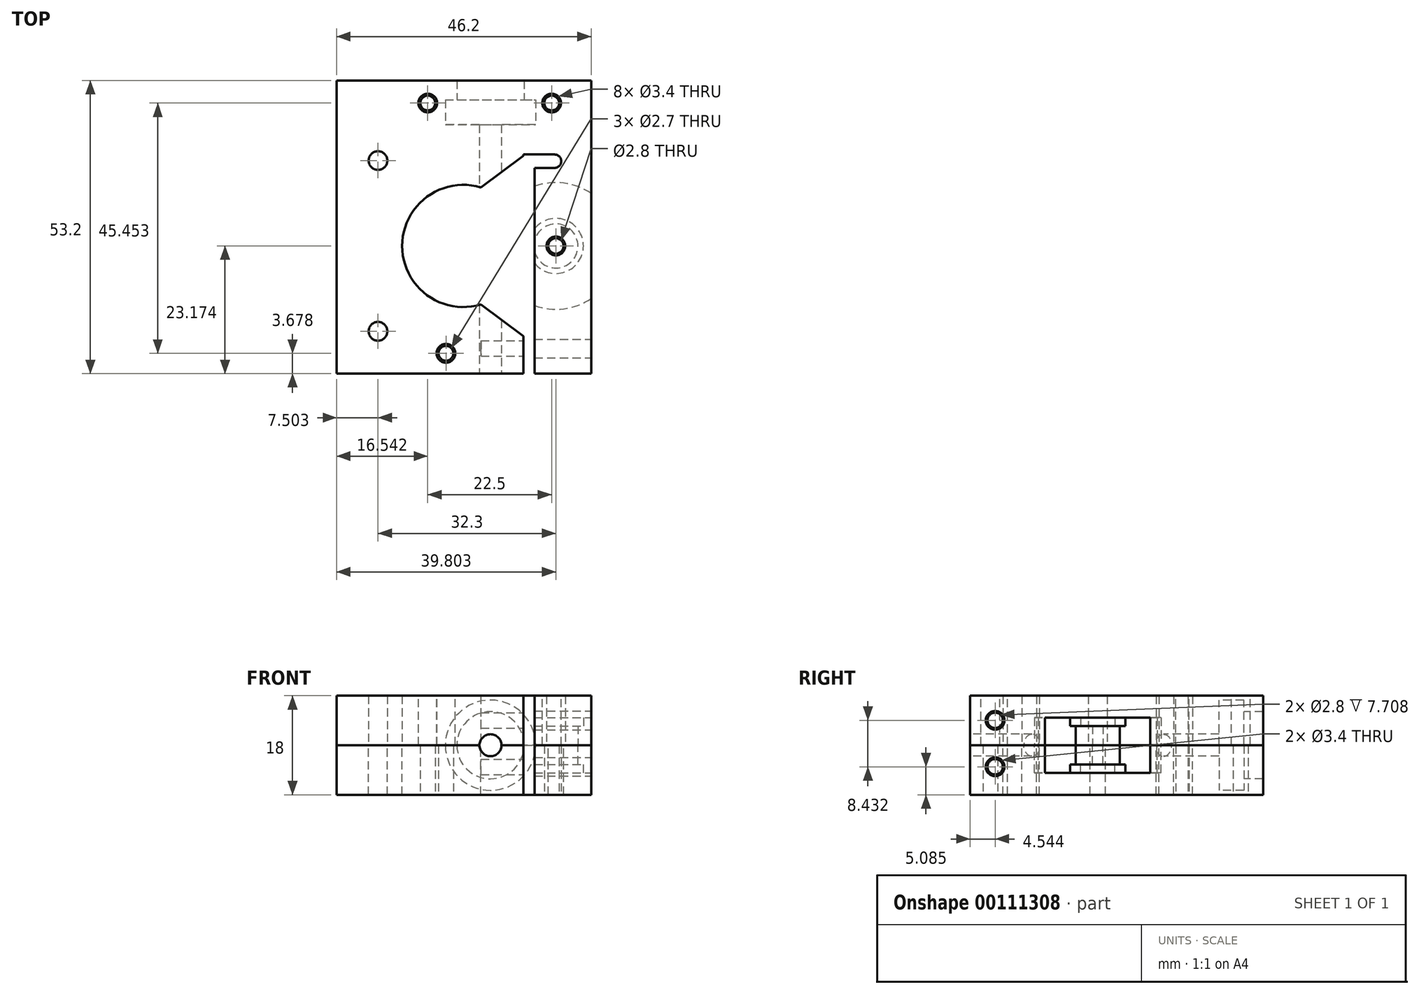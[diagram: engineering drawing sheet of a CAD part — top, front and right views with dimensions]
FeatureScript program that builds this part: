
annotation { "Feature Type Name" : "Feature", "Feature Type Description" : "" }
export const myFeature = defineFeature(function(context is Context, id is Id, definition is map)
    precondition{}
    {
        {
            var Q0;
            Q0=qCreatedBy(makeId("Top.planeOp"),FACE);
            var sketch = newSketch(context, id + "F0", { "sketchPlane" : qUnion([Q0])});
            skLineSegment(sketch, "E0", {"start": v(-24.43, 35.85) * mm, "end": v(-24.43, -17.36) * mm});
            skLineSegment(sketch, "E1", {"start": v(-24.43, -17.36) * mm, "end": v(-24.43, -17.36) * mm});
            skLineSegment(sketch, "E2", {"start": v(-24.43, -17.36) * mm, "end": v(-24.43, -17.35) * mm});
            skLineSegment(sketch, "E3", {"start": v(-24.43, -17.35) * mm, "end": v(9.48, -17.35) * mm});
            skLineSegment(sketch, "E4", {"start": v(9.48, -17.35) * mm, "end": v(9.48, 22.43) * mm});
            skLineSegment(sketch, "E5", {"start": v(9.48, 22.43) * mm, "end": v(15.14, 22.43) * mm});
            skLineSegment(sketch, "E6", {"start": v(15.14, 20) * mm, "end": v(11.48, 20) * mm});
            skLineSegment(sketch, "E7", {"start": v(11.48, 20) * mm, "end": v(11.48, -17.35) * mm});
            skLineSegment(sketch, "E8", {"start": v(11.48, -17.35) * mm, "end": v(21.77, -17.35) * mm});
            skLineSegment(sketch, "E9", {"start": v(21.77, -17.35) * mm, "end": v(21.77, 35.85) * mm});
            skLineSegment(sketch, "E10", {"start": v(21.77, 35.85) * mm, "end": v(-24.43, 35.85) * mm});
            skCircle(sketch, "E11", {"center": v(-7.89, 31.78) * mm, "radius": 1.35 * mm});
            skCircle(sketch, "E12", {"center": v(14.61, 31.78) * mm, "radius": 1.35 * mm});
            skCircle(sketch, "E13", {"center": v(-4.59, -13.67) * mm, "radius": 1.35 * mm});
            skArc(sketch, "E14", {"start": v(15.14, 20) * mm, "mid": v(16.35, 21.21) * mm, "end": v(15.14, 22.43) * mm});
            skCircle(sketch, "E15", {"center": v(-7.89, 31.78) * mm, "radius": 1.7 * mm});
            skCircle(sketch, "E16", {"center": v(14.61, 31.78) * mm, "radius": 1.7 * mm});
            skCircle(sketch, "E17", {"center": v(-4.59, -13.67) * mm, "radius": 1.7 * mm});
            skSolve(sketch);
        }
        {
            var Q0;
            Q0=makeQuery(id+"F0.imprint","IMPRINT",FACE,{"disambiguationData":[TD([[makeQuery(id+"F0.imprint","IMPRINT",EDGE,{"derivedFrom":sQuery(id+"F0.wireOp",EDGE,"E0")}),1.0]])]});
            var Q1;
            Q1=makeQuery(id+"F0.imprint","IMPRINT",FACE,{"disambiguationData":[TD([[makeQuery(id+"F0.imprint","IMPRINT",EDGE,{"derivedFrom":sQuery(id+"F0.wireOp",EDGE,"E11")}),-1.0]])]});
            var Q2;
            Q2=makeQuery(id+"F0.imprint","IMPRINT",FACE,{"disambiguationData":[TD([[makeQuery(id+"F0.imprint","IMPRINT",EDGE,{"derivedFrom":sQuery(id+"F0.wireOp",EDGE,"E12")}),-1.0]])]});
            var Q3;
            Q3=makeQuery(id+"F0.imprint","IMPRINT",FACE,{"disambiguationData":[TD([[makeQuery(id+"F0.imprint","IMPRINT",EDGE,{"derivedFrom":sQuery(id+"F0.wireOp",EDGE,"E13")}),-1.0]])]});
            extrude(context, id + "F1", {"entities" : qUnion([Q0, Q1, Q2, Q3]), "depth" : 9 * mm});
        }
        {
            var Q0;
            Q0=makeQuery(id+"F1.opExtrude","CAP_FACE",FACE,{"disambiguationData":[OSD([sQuery(id+"F0.wireOp",EDGE,"E0"),sQuery(id+"F0.wireOp",EDGE,"E1"),sQuery(id+"F0.wireOp",EDGE,"E2"),sQuery(id+"F0.wireOp",EDGE,"E3"),sQuery(id+"F0.wireOp",EDGE,"E4"),sQuery(id+"F0.wireOp",EDGE,"E5"),sQuery(id+"F0.wireOp",EDGE,"E6"),sQuery(id+"F0.wireOp",EDGE,"E7"),sQuery(id+"F0.wireOp",EDGE,"E8"),sQuery(id+"F0.wireOp",EDGE,"E9"),sQuery(id+"F0.wireOp",EDGE,"E10"),sQuery(id+"F0.wireOp",EDGE,"604cad85-587a-4b7d-8070-06f4cba85480"),sQuery(id+"F0.wireOp",EDGE,"6e5e38c1-5bff-4efe-a8c5-b84022f0a049"),sQuery(id+"F0.wireOp",EDGE,"b8144507-9dd7-4af4-87a3-7b649dd00ae6"),sQuery(id+"F0.wireOp",EDGE,"b9c2cb7c-5e58-4995-888e-a78f0403fbb5"),sQuery(id+"F0.wireOp",EDGE,"885990ab-7576-4c23-8475-595d2769e284"),sQuery(id+"F0.wireOp",EDGE,"E11"),sQuery(id+"F0.wireOp",EDGE,"E12"),sQuery(id+"F0.wireOp",EDGE,"E13"),sQuery(id+"F0.wireOp",EDGE,"E14")])],"isStart":false});
            var sketch = newSketch(context, id + "F2", { "sketchPlane" : qUnion([Q0])});
            skCircle(sketch, "E18", {"center": v(-1.43, 5.82) * mm, "radius": 11.1 * mm});
            skCircle(sketch, "E19", {"center": v(-16.93, 21.32) * mm, "radius": 1.7 * mm});
            skCircle(sketch, "E20", {"center": v(-16.93, -9.68) * mm, "radius": 1.7 * mm});
            skSolve(sketch);
        }
        {
            var Q0;
            Q0=qSketchRegion(id+"F2",true);
            extrude(context, id + "F3", {"entities" : qUnion([Q0]), "operationType" : NewBodyOperationType.REMOVE, "endBound" : BoundingType.THROUGH_ALL, "oppositeDirection" : true, "depth" : 25 * mm});
        }
        {
            var Q0;
            Q0=makeQuery(id+"F1.opExtrude","CAP_FACE",FACE,{"disambiguationData":[OSD([sQuery(id+"F0.wireOp",EDGE,"E0"),sQuery(id+"F0.wireOp",EDGE,"E1"),sQuery(id+"F0.wireOp",EDGE,"E2"),sQuery(id+"F0.wireOp",EDGE,"E3"),sQuery(id+"F0.wireOp",EDGE,"E4"),sQuery(id+"F0.wireOp",EDGE,"E5"),sQuery(id+"F0.wireOp",EDGE,"E6"),sQuery(id+"F0.wireOp",EDGE,"E7"),sQuery(id+"F0.wireOp",EDGE,"E8"),sQuery(id+"F0.wireOp",EDGE,"E9"),sQuery(id+"F0.wireOp",EDGE,"E10"),sQuery(id+"F0.wireOp",EDGE,"604cad85-587a-4b7d-8070-06f4cba85480"),sQuery(id+"F0.wireOp",EDGE,"6e5e38c1-5bff-4efe-a8c5-b84022f0a049"),sQuery(id+"F0.wireOp",EDGE,"E11"),sQuery(id+"F0.wireOp",EDGE,"E12"),sQuery(id+"F0.wireOp",EDGE,"E13"),sQuery(id+"F0.wireOp",EDGE,"E14")])],"isStart":false});
            var sketch = newSketch(context, id + "F4", { "sketchPlane" : qUnion([Q0])});
            skCircle(sketch, "E21", {"center": v(15.37, 5.82) * mm, "radius": 11.5 * mm});
            skCircle(sketch, "E22", {"center": v(15.37, 5.82) * mm, "radius": 5 * mm});
            skCircle(sketch, "E23", {"center": v(15.37, 5.82) * mm, "radius": 4 * mm});
            skLineSegment(sketch, "E24", {"start": v(-1.43, 5.82) * mm, "end": v(32.17, 5.82) * mm, "construction": true});
            skCircle(sketch, "E25", {"center": v(15.37, 5.82) * mm, "radius": 1.4 * mm});
            skCircle(sketch, "E26", {"center": v(15.37, 5.82) * mm, "radius": 1.7 * mm});
            skSolve(sketch);
        }
        {
            var Q0;
            Q0=makeQuery(id+"F4.imprint","IMPRINT",FACE,{"disambiguationData":[TD([[makeQuery(id+"F4.imprint","IMPRINT",EDGE,{"derivedFrom":sQuery(id+"F4.wireOp",EDGE,"E22")}),-1.0]])]});
            extrude(context, id + "F5", {"entities" : qUnion([Q0]), "operationType" : NewBodyOperationType.REMOVE, "oppositeDirection" : true, "depth" : 5 * mm});
        }
        {
            var Q0;
            Q0=makeQuery(id+"F4.imprint","IMPRINT",FACE,{"disambiguationData":[TD([[makeQuery(id+"F4.imprint","IMPRINT",EDGE,{"derivedFrom":sQuery(id+"F4.wireOp",EDGE,"E22")}),1.0]])]});
            var Q1;
            Q1=makeQuery(id+"F4.imprint","IMPRINT",FACE,{"disambiguationData":[TD([[makeQuery(id+"F4.imprint","IMPRINT",EDGE,{"derivedFrom":sQuery(id+"F4.wireOp",EDGE,"E23")}),-1.0]])]});
            extrude(context, id + "F6", {"entities" : qUnion([Q0, Q1]), "operationType" : NewBodyOperationType.REMOVE, "oppositeDirection" : true, "depth" : 3.5 * mm});
        }
        {
            var Q0;
            {var subQ0=sQuery(id+"F0.wireOp",EDGE,"E0");var subQ1=sQuery(id+"F0.wireOp",EDGE,"E1");var subQ2=sQuery(id+"F0.wireOp",EDGE,"E2");var subQ3=sQuery(id+"F0.wireOp",EDGE,"E3");var subQ4=sQuery(id+"F0.wireOp",EDGE,"E4");var subQ5=sQuery(id+"F0.wireOp",EDGE,"E5");var subQ6=sQuery(id+"F0.wireOp",EDGE,"E6");var subQ7=sQuery(id+"F0.wireOp",EDGE,"E7");var subQ8=sQuery(id+"F0.wireOp",EDGE,"E9");var subQ9=sQuery(id+"F0.wireOp",EDGE,"E10");var subQ10=sQuery(id+"F0.wireOp",EDGE,"604cad85-587a-4b7d-8070-06f4cba85480");var subQ11=sQuery(id+"F0.wireOp",EDGE,"6e5e38c1-5bff-4efe-a8c5-b84022f0a049");var subQ12=sQuery(id+"F0.wireOp",EDGE,"E11");var subQ13=sQuery(id+"F0.wireOp",EDGE,"E12");var subQ14=sQuery(id+"F0.wireOp",EDGE,"E13");var subQ15=sQuery(id+"F0.wireOp",EDGE,"E14");Q0=makeQuery(id+"F5.boolean.opBoolean","SPLIT",FACE,{"disambiguationData":[TD([makeQuery(id+"F1.opExtrude","SWEPT_FACE",FACE,{"disambiguationData":[OSD([subQ0])]})])],"derivedFrom":makeQuery(id+"F1.opExtrude","CAP_FACE",FACE,{"disambiguationData":[OSD([subQ0,subQ1,subQ2,subQ3,subQ4,subQ5,subQ6,subQ7,sQuery(id+"F0.wireOp",EDGE,"E8"),subQ8,subQ9,subQ10,subQ11,subQ12,subQ13,subQ14,subQ15])],"isStart":false})});}
            var sketch = newSketch(context, id + "F7", { "sketchPlane" : qUnion([Q0])});
            skLineSegment(sketch, "E27", {"start": v(3.5, 13.61) * mm, "end": v(3.5, 36.54) * mm});
            skLineSegment(sketch, "E28", {"start": v(-1.43, 5.82) * mm, "end": v(31.4, 5.82) * mm, "construction": true});
            skLineSegment(sketch, "E29.0.MirrorCS", {"start": v(1.5, -6.46) * mm, "end": v(1.5, -6.46) * mm});
            skLineSegment(sketch, "E29.1.MirrorCS", {"start": v(3.5, -1.96) * mm, "end": v(3.5, -24.9) * mm});
            skLineSegment(sketch, "E29.2.MirrorCS", {"start": v(1.5, -11.66) * mm, "end": v(1.5, -6.46) * mm});
            skLineSegment(sketch, "E29.3.MirrorCS", {"start": v(1.9, -1.96) * mm, "end": v(3.5, -1.96) * mm});
            skLineSegment(sketch, "E29.4.MirrorCS", {"start": v(1.9, -2.25) * mm, "end": v(1.5, -2.25) * mm});
            skLineSegment(sketch, "E29.5.MirrorCS", {"start": v(1.5, -6.46) * mm, "end": v(1.5, -2.25) * mm});
            skLineSegment(sketch, "E30", {"start": v(-2.6, 36.54) * mm, "end": v(-2.6, 32.34) * mm});
            skLineSegment(sketch, "E31", {"start": v(-2.6, 32.34) * mm, "end": v(-4.7, 32.34) * mm});
            skLineSegment(sketch, "E32", {"start": v(-4.7, 32.34) * mm, "end": v(-4.7, 27.84) * mm});
            skLineSegment(sketch, "E33", {"start": v(-4.7, 27.84) * mm, "end": v(1.5, 27.84) * mm});
            skLineSegment(sketch, "E34", {"start": v(-2.6, 36.54) * mm, "end": v(3.5, 36.54) * mm});
            skLineSegment(sketch, "E35", {"start": v(1.5, 27.84) * mm, "end": v(1.5, 13.61) * mm});
            skLineSegment(sketch, "E36", {"start": v(1.5, 13.61) * mm, "end": v(3.5, 13.61) * mm});
            skLineSegment(sketch, "E37", {"start": v(1.9, -2.25) * mm, "end": v(1.9, -1.96) * mm});
            skLineSegment(sketch, "E38", {"start": v(1.5, -11.66) * mm, "end": v(1.5, -11.66) * mm});
            skLineSegment(sketch, "E39", {"start": v(1.5, -11.66) * mm, "end": v(1.5, -24.9) * mm});
            skLineSegment(sketch, "E40", {"start": v(1.5, -24.9) * mm, "end": v(3.5, -24.9) * mm});
            skSolve(sketch);
        }
        {
            var Q0;
            Q0=qSketchRegion(id+"F7",true);
            var Q1;
            Q1=sQuery(id+"F7.wireOp",EDGE,"E27");
            revolve(context, id + "F8", {"entities" : qUnion([Q0]), "axis" : qUnion([Q1]), "revolveType" : RevolveType.FULL});
        }
        {
            var Q0;
            Q0=makeQuery(id+"F8.opRevolve","SWEPT_BODY",BODY,{"disambiguationData":[OSD([sQuery(id+"F7.wireOp",EDGE,"0e4a01cc-4869-4b9d-8ca2-1c94110d196d"),sQuery(id+"F7.wireOp",EDGE,"4d913e13-2244-4a79-84d2-82f6c5de00b3"),sQuery(id+"F7.wireOp",EDGE,"1203443b-fa58-4cec-9fe4-144960d3b7c2"),sQuery(id+"F7.wireOp",EDGE,"f73e5a92-9274-40af-91db-ab5fa52ec61f"),sQuery(id+"F7.wireOp",EDGE,"4cc6588a-36a6-4115-9f4e-735cf5f17870"),sQuery(id+"F7.wireOp",EDGE,"E27"),sQuery(id+"F7.wireOp",EDGE,"0bbee7b9-97e0-41c3-ac0e-625151f8027d")])]});
            var Q1;
            Q1=makeQuery(id+"F1.opExtrude","SWEPT_BODY",BODY,{"disambiguationData":[OSD([sQuery(id+"F0.wireOp",EDGE,"E0"),sQuery(id+"F0.wireOp",EDGE,"E1"),sQuery(id+"F0.wireOp",EDGE,"E2"),sQuery(id+"F0.wireOp",EDGE,"E3"),sQuery(id+"F0.wireOp",EDGE,"E4"),sQuery(id+"F0.wireOp",EDGE,"E5"),sQuery(id+"F0.wireOp",EDGE,"E6"),sQuery(id+"F0.wireOp",EDGE,"E7"),sQuery(id+"F0.wireOp",EDGE,"E8"),sQuery(id+"F0.wireOp",EDGE,"E9"),sQuery(id+"F0.wireOp",EDGE,"E10"),sQuery(id+"F0.wireOp",EDGE,"604cad85-587a-4b7d-8070-06f4cba85480"),sQuery(id+"F0.wireOp",EDGE,"6e5e38c1-5bff-4efe-a8c5-b84022f0a049"),sQuery(id+"F0.wireOp",EDGE,"E11"),sQuery(id+"F0.wireOp",EDGE,"E12"),sQuery(id+"F0.wireOp",EDGE,"E13"),sQuery(id+"F0.wireOp",EDGE,"E14")])]});
            booleanBodies(context, id + "F9", {"operationType" : BooleanOperationType.SUBTRACTION, "tools" : qUnion([Q0]), "targets" : qUnion([Q1]), "keepTools" : true});
        }
        {
            var Q0;
            Q0=makeQuery(id+"F8.opRevolve","SWEPT_BODY",BODY,{"disambiguationData":[OSD([sQuery(id+"F7.wireOp",EDGE,"E29.0.MirrorCS"),sQuery(id+"F7.wireOp",EDGE,"E29.1.MirrorCS"),sQuery(id+"F7.wireOp",EDGE,"E29.2.MirrorCS"),sQuery(id+"F7.wireOp",EDGE,"E29.3.MirrorCS"),sQuery(id+"F7.wireOp",EDGE,"E29.4.MirrorCS"),sQuery(id+"F7.wireOp",EDGE,"E29.5.MirrorCS"),sQuery(id+"F7.wireOp",EDGE,"E29.6.MirrorCS")])]});
            var Q1;
            Q1=makeQuery(id+"F1.opExtrude","SWEPT_BODY",BODY,{"disambiguationData":[OSD([sQuery(id+"F0.wireOp",EDGE,"E0"),sQuery(id+"F0.wireOp",EDGE,"E1"),sQuery(id+"F0.wireOp",EDGE,"E2"),sQuery(id+"F0.wireOp",EDGE,"E3"),sQuery(id+"F0.wireOp",EDGE,"E4"),sQuery(id+"F0.wireOp",EDGE,"E5"),sQuery(id+"F0.wireOp",EDGE,"E6"),sQuery(id+"F0.wireOp",EDGE,"E7"),sQuery(id+"F0.wireOp",EDGE,"E8"),sQuery(id+"F0.wireOp",EDGE,"E9"),sQuery(id+"F0.wireOp",EDGE,"E10"),sQuery(id+"F0.wireOp",EDGE,"604cad85-587a-4b7d-8070-06f4cba85480"),sQuery(id+"F0.wireOp",EDGE,"6e5e38c1-5bff-4efe-a8c5-b84022f0a049"),sQuery(id+"F0.wireOp",EDGE,"E11"),sQuery(id+"F0.wireOp",EDGE,"E12"),sQuery(id+"F0.wireOp",EDGE,"E13"),sQuery(id+"F0.wireOp",EDGE,"E14")])]});
            booleanBodies(context, id + "F10", {"operationType" : BooleanOperationType.SUBTRACTION, "tools" : qUnion([Q0]), "targets" : qUnion([Q1]), "keepTools" : true});
        }
        {
            var Q0;
            Q0=qSketchRegion(id+"F0",true);
            extrude(context, id + "F11", {"entities" : qUnion([Q0]), "oppositeDirection" : true, "depth" : 9 * mm});
        }
        {
            var Q0;
            Q0=makeQuery(id+"F11.opExtrude","SWEPT_BODY",BODY,{"disambiguationData":[OSD([sQuery(id+"F0.wireOp",EDGE,"E0"),sQuery(id+"F0.wireOp",EDGE,"E3"),sQuery(id+"F0.wireOp",EDGE,"E4"),sQuery(id+"F0.wireOp",EDGE,"E5"),sQuery(id+"F0.wireOp",EDGE,"E6"),sQuery(id+"F0.wireOp",EDGE,"E7"),sQuery(id+"F0.wireOp",EDGE,"E8"),sQuery(id+"F0.wireOp",EDGE,"E9"),sQuery(id+"F0.wireOp",EDGE,"E10"),sQuery(id+"F0.wireOp",EDGE,"E11"),sQuery(id+"F0.wireOp",EDGE,"E12"),sQuery(id+"F0.wireOp",EDGE,"E13"),sQuery(id+"F0.wireOp",EDGE,"E14")])]});
            transform(context, id + "F12", {"entities" : qUnion([Q0]), "transformType" : TransformType.TRANSLATION_3D, "dx" : 0 * mm, "dy" : 0 * mm, "dz" : 18 * mm, "makeCopy" : false});
        }
        {
            var Q0;
            Q0=qSketchRegion(id+"F2",true);
            extrude(context, id + "F13", {"entities" : qUnion([Q0]), "operationType" : NewBodyOperationType.REMOVE, "endBound" : BoundingType.THROUGH_ALL, "depth" : 25 * mm});
        }
        {
            var Q0;
            {var subQ3=sQuery(id+"F4.wireOp",EDGE,"E21");var subQ7=makeQuery(id+"F1.opExtrude","CAP_EDGE",EDGE,{"disambiguationData":[OSD([sQuery(id+"F0.wireOp",EDGE,"E9")])],"isStart":false});var subQ9=makeQuery(id+"F4.imprint","INTERSECT",VERTEX,{"disambiguationData":[OD(0.0)],"derivedFrom":[subQ7,subQ3]});Q0=makeQuery(id+"F4.imprint","IMPRINT",FACE,{"disambiguationData":[TD([[makeQuery(id+"F4.imprint","IMPRINT",EDGE,{"disambiguationData":[TD([[subQ9,-1.0]])],"derivedFrom":subQ3}),1.0]])]});}
            extrude(context, id + "F14", {"entities" : qUnion([Q0]), "operationType" : NewBodyOperationType.REMOVE, "depth" : 5 * mm});
        }
        {
            var Q0;
            Q0=makeQuery(id+"F4.imprint","IMPRINT",FACE,{"disambiguationData":[TD([[makeQuery(id+"F4.imprint","IMPRINT",EDGE,{"derivedFrom":sQuery(id+"F4.wireOp",EDGE,"E23")}),-1.0]])]});
            extrude(context, id + "F15", {"entities" : qUnion([Q0]), "operationType" : NewBodyOperationType.REMOVE, "depth" : 3.5 * mm});
        }
        {
            var Q0;
            Q0=makeQuery(id+"F8.opRevolve","SWEPT_BODY",BODY,{"disambiguationData":[OSD([sQuery(id+"F7.wireOp",EDGE,"0e4a01cc-4869-4b9d-8ca2-1c94110d196d"),sQuery(id+"F7.wireOp",EDGE,"4d913e13-2244-4a79-84d2-82f6c5de00b3"),sQuery(id+"F7.wireOp",EDGE,"1203443b-fa58-4cec-9fe4-144960d3b7c2"),sQuery(id+"F7.wireOp",EDGE,"f73e5a92-9274-40af-91db-ab5fa52ec61f"),sQuery(id+"F7.wireOp",EDGE,"4cc6588a-36a6-4115-9f4e-735cf5f17870"),sQuery(id+"F7.wireOp",EDGE,"E27"),sQuery(id+"F7.wireOp",EDGE,"0bbee7b9-97e0-41c3-ac0e-625151f8027d")])]});
            var Q1;
            Q1=makeQuery(id+"F11.opExtrude","SWEPT_BODY",BODY,{"disambiguationData":[OSD([sQuery(id+"F0.wireOp",EDGE,"E0"),sQuery(id+"F0.wireOp",EDGE,"E3"),sQuery(id+"F0.wireOp",EDGE,"E4"),sQuery(id+"F0.wireOp",EDGE,"E5"),sQuery(id+"F0.wireOp",EDGE,"E6"),sQuery(id+"F0.wireOp",EDGE,"E7"),sQuery(id+"F0.wireOp",EDGE,"E8"),sQuery(id+"F0.wireOp",EDGE,"E9"),sQuery(id+"F0.wireOp",EDGE,"E10"),sQuery(id+"F0.wireOp",EDGE,"E11"),sQuery(id+"F0.wireOp",EDGE,"E12"),sQuery(id+"F0.wireOp",EDGE,"E13"),sQuery(id+"F0.wireOp",EDGE,"E14")])]});
            booleanBodies(context, id + "F16", {"operationType" : BooleanOperationType.SUBTRACTION, "tools" : qUnion([Q0]), "targets" : qUnion([Q1])});
        }
        {
            var Q0;
            Q0=makeQuery(id+"F8.opRevolve","SWEPT_BODY",BODY,{"disambiguationData":[OSD([sQuery(id+"F7.wireOp",EDGE,"E29.0.MirrorCS"),sQuery(id+"F7.wireOp",EDGE,"E29.1.MirrorCS"),sQuery(id+"F7.wireOp",EDGE,"E29.2.MirrorCS"),sQuery(id+"F7.wireOp",EDGE,"E29.3.MirrorCS"),sQuery(id+"F7.wireOp",EDGE,"E29.4.MirrorCS"),sQuery(id+"F7.wireOp",EDGE,"E29.5.MirrorCS"),sQuery(id+"F7.wireOp",EDGE,"E29.6.MirrorCS")])]});
            var Q1;
            Q1=makeQuery(id+"F11.opExtrude","SWEPT_BODY",BODY,{"disambiguationData":[OSD([sQuery(id+"F0.wireOp",EDGE,"E0"),sQuery(id+"F0.wireOp",EDGE,"E3"),sQuery(id+"F0.wireOp",EDGE,"E4"),sQuery(id+"F0.wireOp",EDGE,"E5"),sQuery(id+"F0.wireOp",EDGE,"E6"),sQuery(id+"F0.wireOp",EDGE,"E7"),sQuery(id+"F0.wireOp",EDGE,"E8"),sQuery(id+"F0.wireOp",EDGE,"E9"),sQuery(id+"F0.wireOp",EDGE,"E10"),sQuery(id+"F0.wireOp",EDGE,"E11"),sQuery(id+"F0.wireOp",EDGE,"E12"),sQuery(id+"F0.wireOp",EDGE,"E13"),sQuery(id+"F0.wireOp",EDGE,"E14")])]});
            booleanBodies(context, id + "F17", {"operationType" : BooleanOperationType.SUBTRACTION, "tools" : qUnion([Q0]), "targets" : qUnion([Q1])});
        }
        {
            var Q0;
            Q0=makeQuery(id+"F11.opExtrude","SWEPT_FACE",FACE,{"disambiguationData":[OSD([sQuery(id+"F0.wireOp",EDGE,"E9")])]});
            var sketch = newSketch(context, id + "F18", { "sketchPlane" : qUnion([Q0])});
            skCircle(sketch, "E41", {"center": v(-12.8, 13.52) * mm, "radius": 1.7 * mm});
            skCircle(sketch, "E42", {"center": v(-12.8, 13.52) * mm, "radius": 1.4 * mm});
            skCircle(sketch, "E43", {"center": v(-12.8, 5.09) * mm, "radius": 1.7 * mm});
            skCircle(sketch, "E44", {"center": v(-12.8, 5.09) * mm, "radius": 1.4 * mm});
            skSolve(sketch);
        }
        {
            var Q0;
            Q0=makeQuery(id+"F18.imprint","IMPRINT",FACE,{"disambiguationData":[TD([[makeQuery(id+"F18.imprint","IMPRINT",EDGE,{"derivedFrom":sQuery(id+"F18.wireOp",EDGE,"E42")}),1.0]])]});
            extrude(context, id + "F19", {"entities" : qUnion([Q0]), "operationType" : NewBodyOperationType.REMOVE, "oppositeDirection" : true, "depth" : 20 * mm});
        }
        {
            var Q0;
            Q0=makeQuery(id+"F18.imprint","IMPRINT",FACE,{"disambiguationData":[TD([[makeQuery(id+"F18.imprint","IMPRINT",EDGE,{"derivedFrom":sQuery(id+"F18.wireOp",EDGE,"E41")}),1.0]])]});
            extrude(context, id + "F20", {"entities" : qUnion([Q0]), "operationType" : NewBodyOperationType.REMOVE, "oppositeDirection" : true, "depth" : 11 * mm});
        }
        {
            var Q0;
            Q0=makeQuery(id+"F18.imprint","IMPRINT",FACE,{"disambiguationData":[TD([[makeQuery(id+"F18.imprint","IMPRINT",EDGE,{"derivedFrom":sQuery(id+"F18.wireOp",EDGE,"E44")}),1.0]])]});
            extrude(context, id + "F21", {"entities" : qUnion([Q0]), "operationType" : NewBodyOperationType.REMOVE, "oppositeDirection" : true, "depth" : 20 * mm});
        }
        {
            var Q0;
            Q0=makeQuery(id+"F18.imprint","IMPRINT",FACE,{"disambiguationData":[TD([[makeQuery(id+"F18.imprint","IMPRINT",EDGE,{"derivedFrom":sQuery(id+"F18.wireOp",EDGE,"E43")}),1.0]])]});
            extrude(context, id + "F22", {"entities" : qUnion([Q0]), "operationType" : NewBodyOperationType.REMOVE, "oppositeDirection" : true, "depth" : 11 * mm});
        }
        {
            var Q0;
            Q0=makeQuery(id+"F4.imprint","IMPRINT",FACE,{"disambiguationData":[TD([[makeQuery(id+"F4.imprint","IMPRINT",EDGE,{"derivedFrom":sQuery(id+"F4.wireOp",EDGE,"E25")}),1.0]])]});
            extrude(context, id + "F23", {"entities" : qUnion([Q0]), "operationType" : NewBodyOperationType.REMOVE, "endBound" : BoundingType.THROUGH_ALL, "oppositeDirection" : true, "depth" : 25 * mm});
        }
        {
            var Q0;
            Q0=makeQuery(id+"F4.imprint","IMPRINT",FACE,{"disambiguationData":[TD([[makeQuery(id+"F4.imprint","IMPRINT",EDGE,{"derivedFrom":sQuery(id+"F4.wireOp",EDGE,"E25")}),1.0]])]});
            var Q1;
            Q1=makeQuery(id+"F4.imprint","IMPRINT",FACE,{"disambiguationData":[TD([[makeQuery(id+"F4.imprint","IMPRINT",EDGE,{"derivedFrom":sQuery(id+"F4.wireOp",EDGE,"E25")}),-1.0]])]});
            extrude(context, id + "F24", {"entities" : qUnion([Q0, Q1]), "operationType" : NewBodyOperationType.REMOVE, "endBound" : BoundingType.THROUGH_ALL, "depth" : 25 * mm});
        }
        {
            var Q0;
            Q0=makeQuery(id+"F3.boolean.opBoolean","INTERSECT",EDGE,{"disambiguationData":[OD(0.0)],"derivedFrom":[makeQuery(id+"F1.opExtrude","SWEPT_FACE",FACE,{"disambiguationData":[OSD([sQuery(id+"F0.wireOp",EDGE,"E4")])]}),makeQuery(id+"F3.opExtrude","SWEPT_FACE",FACE,{"disambiguationData":[OSD([sQuery(id+"F2.wireOp",EDGE,"E18")])]})]});
            var Q1;
            Q1=makeQuery(id+"F3.boolean.opBoolean","INTERSECT",EDGE,{"disambiguationData":[OD(1.0)],"derivedFrom":[makeQuery(id+"F1.opExtrude","SWEPT_FACE",FACE,{"disambiguationData":[OSD([sQuery(id+"F0.wireOp",EDGE,"E4")])]}),makeQuery(id+"F3.opExtrude","SWEPT_FACE",FACE,{"disambiguationData":[OSD([sQuery(id+"F2.wireOp",EDGE,"E18")])]})]});
            var Q2;
            Q2=makeQuery(id+"F13.boolean.opBoolean","INTERSECT",EDGE,{"disambiguationData":[OD(1.0)],"derivedFrom":[makeQuery(id+"F11.opExtrude","SWEPT_FACE",FACE,{"disambiguationData":[OSD([sQuery(id+"F0.wireOp",EDGE,"E4")])]}),makeQuery(id+"F13.opExtrude","SWEPT_FACE",FACE,{"disambiguationData":[OSD([sQuery(id+"F2.wireOp",EDGE,"E18")])]})]});
            var Q3;
            Q3=makeQuery(id+"F13.boolean.opBoolean","INTERSECT",EDGE,{"disambiguationData":[OD(0.0)],"derivedFrom":[makeQuery(id+"F11.opExtrude","SWEPT_FACE",FACE,{"disambiguationData":[OSD([sQuery(id+"F0.wireOp",EDGE,"E4")])]}),makeQuery(id+"F13.opExtrude","SWEPT_FACE",FACE,{"disambiguationData":[OSD([sQuery(id+"F2.wireOp",EDGE,"E18")])]})]});
            chamfer(context, id + "F25", {"entities" : qUnion([Q0, Q1, Q2, Q3]), "width" : 6 * mm, "tangentPropagation" : true});
        }
    });
